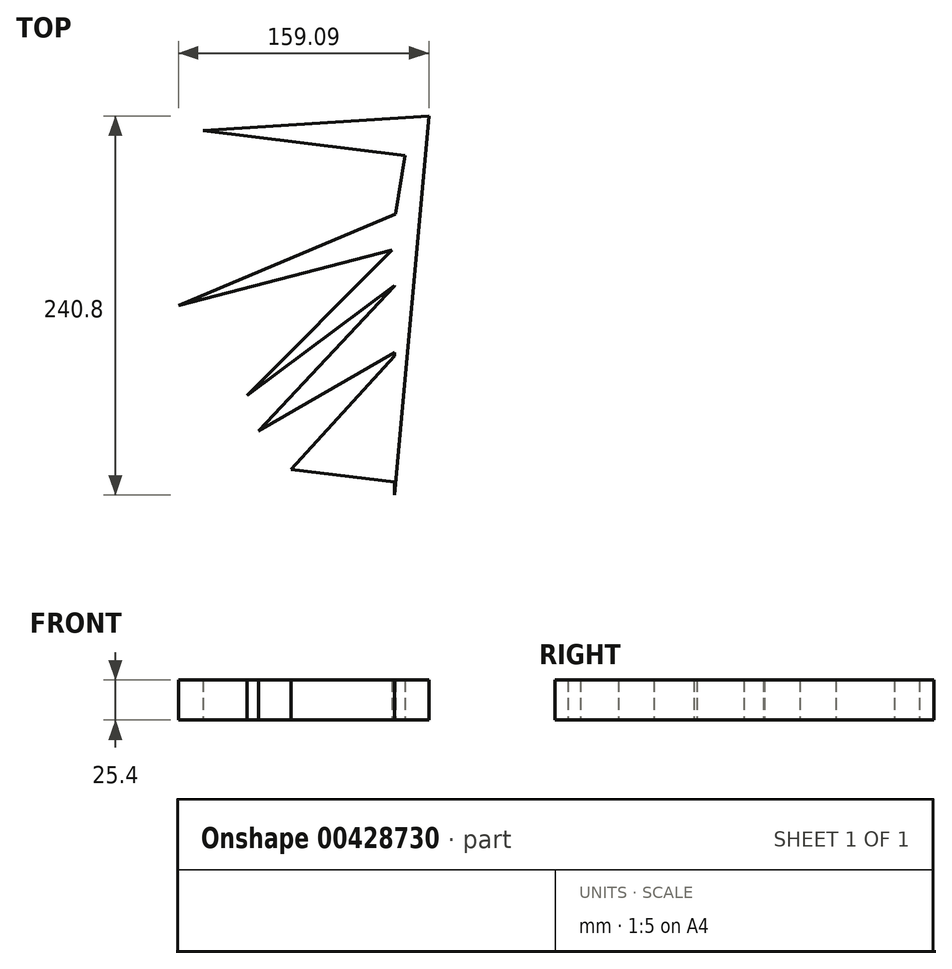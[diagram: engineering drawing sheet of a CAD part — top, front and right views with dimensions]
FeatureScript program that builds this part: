
annotation { "Feature Type Name" : "Feature", "Feature Type Description" : "" }
export const myFeature = defineFeature(function(context is Context, id is Id, definition is map)
    precondition{}
    {
        {
            var Q0;
            Q0=qCreatedBy(makeId("Top.planeOp"),FACE);
            var sketch = newSketch(context, id + "F0", { "sketchPlane" : qUnion([Q0])});
            skLineSegment(sketch, "E0", {"start": v(98.9, 58.28) * mm, "end": v(98.9, -120.23) * mm});
            skLineSegment(sketch, "E1", {"start": v(98.9, -120.23) * mm, "end": v(120.77, 120.57) * mm});
            skLineSegment(sketch, "E2", {"start": v(120.77, 120.57) * mm, "end": v(-22.62, 111.36) * mm});
            skLineSegment(sketch, "E3", {"start": v(-22.62, 111.36) * mm, "end": v(105.82, 95.45) * mm});
            skLineSegment(sketch, "E4", {"start": v(105.82, 95.45) * mm, "end": v(99.5, 58.3) * mm});
            skLineSegment(sketch, "E5", {"start": v(99.5, 58.3) * mm, "end": v(-38.32, 0) * mm});
            skLineSegment(sketch, "E6", {"start": v(-38.32, 0) * mm, "end": v(97.54, 35.37) * mm});
            skLineSegment(sketch, "E7", {"start": v(97.54, 35.37) * mm, "end": v(5.18, -57.13) * mm});
            skLineSegment(sketch, "E8", {"start": v(5.18, -57.13) * mm, "end": v(100.24, 13.9) * mm});
            skLineSegment(sketch, "E9", {"start": v(100.24, 13.9) * mm, "end": v(12.66, -79.67) * mm});
            skLineSegment(sketch, "E10", {"start": v(12.66, -79.67) * mm, "end": v(103, -27.44) * mm});
            skLineSegment(sketch, "E11", {"start": v(103, -27.44) * mm, "end": v(33.43, -103.9) * mm});
            skLineSegment(sketch, "E12", {"start": v(33.43, -103.9) * mm, "end": v(103.37, -112.47) * mm});
            skSolve(sketch);
        }
        {
            var Q0;
            Q0 = qSketchRegion(id + "F0", true);
            extrude(context, id + "F1", {"entities" : qUnion([Q0]), "depth" : 25.4 * mm});
        }
    });
